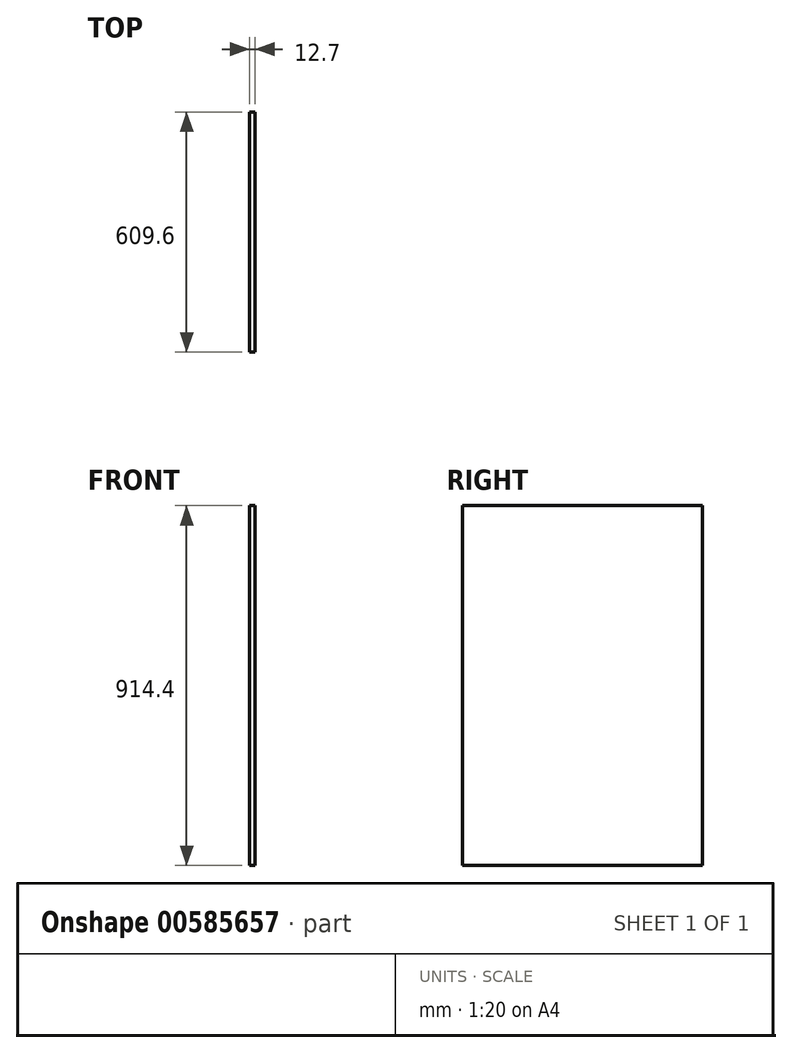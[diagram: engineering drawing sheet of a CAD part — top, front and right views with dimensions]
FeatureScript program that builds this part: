
annotation { "Feature Type Name" : "Feature", "Feature Type Description" : "" }
export const myFeature = defineFeature(function(context is Context, id is Id, definition is map)
    precondition{}
    {
        {
            var Q0;
            Q0=qCreatedBy(makeId("Right.planeOp"),FACE);
            var sketch = newSketch(context, id + "F0", { "sketchPlane" : qUnion([Q0])});
            skLineSegment(sketch, "E0.bottom", {"start": v(0, 0) * mm, "end": v(609.6, 0) * mm});
            skLineSegment(sketch, "E0.top", {"start": v(0, 914.4) * mm, "end": v(609.6, 914.4) * mm});
            skLineSegment(sketch, "E0.left", {"start": v(0, 0) * mm, "end": v(0, 914.4) * mm});
            skLineSegment(sketch, "E0.right", {"start": v(609.6, 0) * mm, "end": v(609.6, 914.4) * mm});
            skSolve(sketch);
        }
        {
            var Q0;
            Q0=qSketchRegion(id+"F0",true);
            extrude(context, id + "F1", {"entities" : qUnion([Q0]), "depth" : 12.7 * mm, "offsetDistance" : 25.4 * mm});
        }
    });
